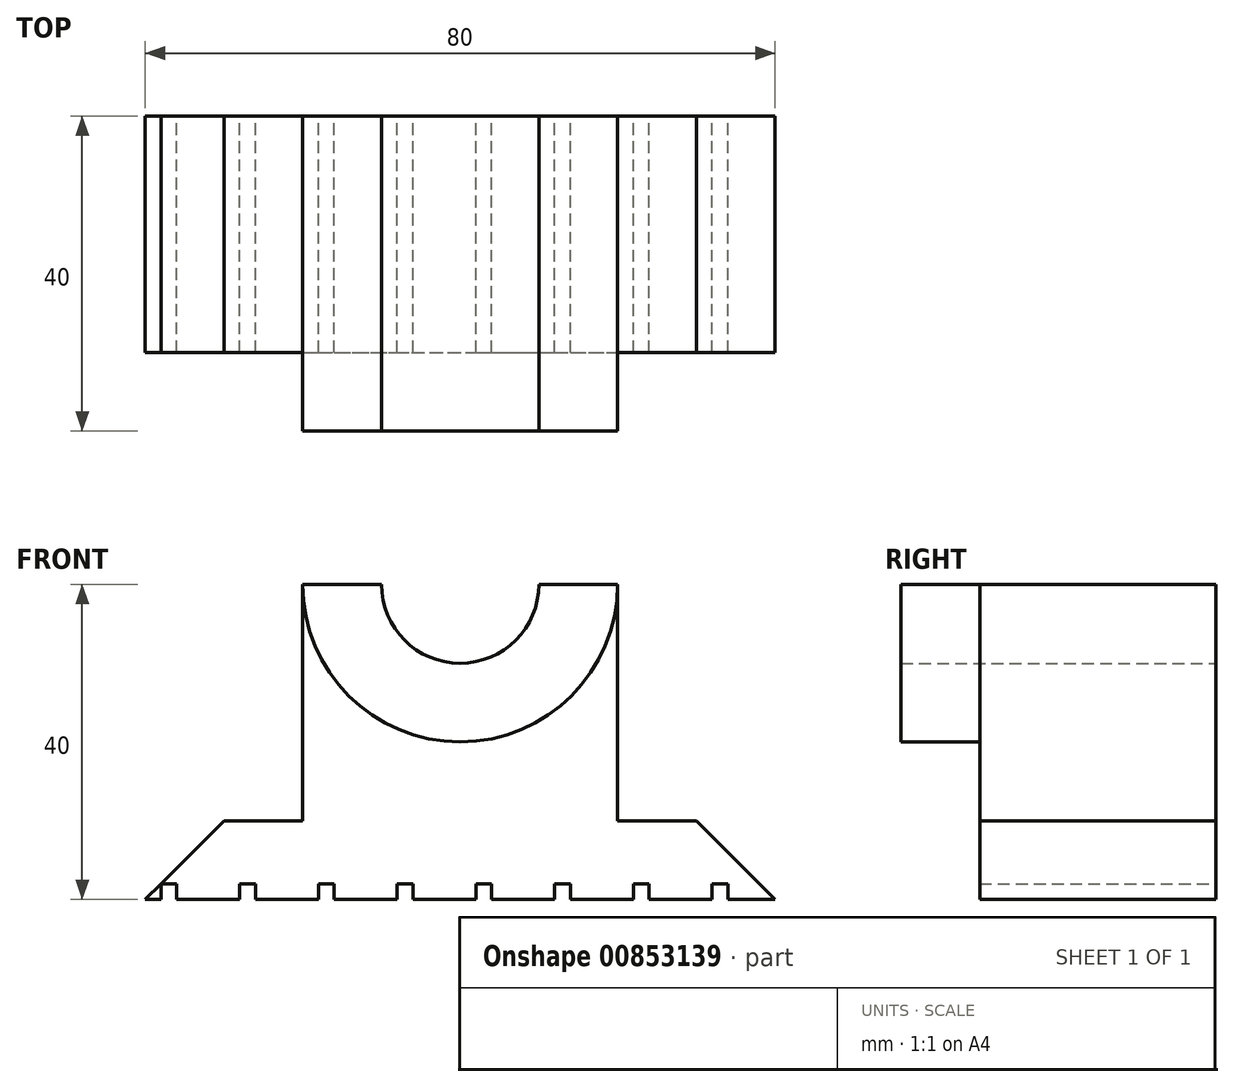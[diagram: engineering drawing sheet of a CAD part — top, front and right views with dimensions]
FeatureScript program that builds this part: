
annotation { "Feature Type Name" : "Feature", "Feature Type Description" : "" }
export const myFeature = defineFeature(function(context is Context, id is Id, definition is map)
    precondition{}
    {
        {
            var Q0;
            Q0=qCreatedBy(makeId("Front.planeOp"),FACE);
            var sketch = newSketch(context, id + "F0", { "sketchPlane" : qUnion([Q0])});
            skLineSegment(sketch, "E0", {"start": v(-40, 0) * mm, "end": v(40, 0) * mm});
            skLineSegment(sketch, "E1", {"start": v(40, 0) * mm, "end": v(30, 10) * mm});
            skLineSegment(sketch, "E2", {"start": v(30, 10) * mm, "end": v(20, 10) * mm});
            skLineSegment(sketch, "E3", {"start": v(20, 10) * mm, "end": v(20, 40) * mm});
            skLineSegment(sketch, "E4", {"start": v(20, 40) * mm, "end": v(10, 40) * mm});
            skLineSegment(sketch, "E5", {"start": v(-20, 40) * mm, "end": v(-20, 10) * mm});
            skLineSegment(sketch, "E6", {"start": v(-20, 10) * mm, "end": v(-30, 10) * mm});
            skLineSegment(sketch, "E7", {"start": v(-30, 10) * mm, "end": v(-40, 0) * mm});
            skArc(sketch, "E8", {"start": v(-10, 40) * mm, "mid": v(0, 30) * mm, "end": v(10, 40) * mm});
            skLineSegment(sketch, "E9.trimOffspring", {"start": v(-10, 40) * mm, "end": v(-20, 40) * mm});
            skSolve(sketch);
        }
        {
            var Q0;
            Q0 = qSketchRegion(id + "F0", true);
            extrude(context, id + "F1", {"entities" : qUnion([Q0]), "depth" : 30 * mm, "offsetDistance" : 25 * mm});
        }
        {
            var Q0;
            Q0=makeQuery(id+"F1.opExtrude","CAP_FACE",FACE,{"disambiguationData":[OSD([sQuery(id+"F0.wireOp",EDGE,"E0"),sQuery(id+"F0.wireOp",EDGE,"E1"),sQuery(id+"F0.wireOp",EDGE,"E2"),sQuery(id+"F0.wireOp",EDGE,"E3"),sQuery(id+"F0.wireOp",EDGE,"E4"),sQuery(id+"F0.wireOp",EDGE,"E5"),sQuery(id+"F0.wireOp",EDGE,"E6"),sQuery(id+"F0.wireOp",EDGE,"E7"),sQuery(id+"F0.wireOp",EDGE,"E8"),sQuery(id+"F0.wireOp",EDGE,"E9.trimOffspring")])],"isStart":false});
            var sketch = newSketch(context, id + "F2", { "sketchPlane" : qUnion([Q0])});
            skArc(sketch, "E10", {"start": v(-20, 40) * mm, "mid": v(0, 20) * mm, "end": v(20, 40) * mm});
            skArc(sketch, "E11", {"start": v(-10, 40) * mm, "mid": v(0, 30) * mm, "end": v(10, 40) * mm});
            skLineSegment(sketch, "E12", {"start": v(-20, 40) * mm, "end": v(-10, 40) * mm});
            skLineSegment(sketch, "E13.trimOffspring", {"start": v(10, 40) * mm, "end": v(20, 40) * mm});
            skSolve(sketch);
        }
        {
            var Q0;
            Q0 = qSketchRegion(id + "F2", true);
            extrude(context, id + "F3", {"entities" : qUnion([Q0]), "operationType" : NewBodyOperationType.ADD, "depth" : 10 * mm, "offsetDistance" : 25 * mm});
        }
        {
            var Q0;
            Q0=makeQuery(id+"F1.opExtrude","SWEPT_FACE",FACE,{"disambiguationData":[OSD([sQuery(id+"F0.wireOp",EDGE,"E0")])]});
            var sketch = newSketch(context, id + "F4", { "sketchPlane" : qUnion([Q0])});
            skLineSegment(sketch, "E14.bottom", {"start": v(-38, 30) * mm, "end": v(-36, 30) * mm});
            skLineSegment(sketch, "E14.top", {"start": v(-38, 0) * mm, "end": v(-36, 0) * mm});
            skLineSegment(sketch, "E14.left", {"start": v(-38, 30) * mm, "end": v(-38, 0) * mm});
            skLineSegment(sketch, "E14.right", {"start": v(-36, 30) * mm, "end": v(-36, 0) * mm});
            skLineSegment(sketch, "E15.1.0.0", {"start": v(-26, 30) * mm, "end": v(-26, 0) * mm});
            skLineSegment(sketch, "E15.1.0.1", {"start": v(-28, 30) * mm, "end": v(-28, 0) * mm});
            skLineSegment(sketch, "E15.1.0.2", {"start": v(-28, 30) * mm, "end": v(-26, 30) * mm});
            skLineSegment(sketch, "E15.1.0.3", {"start": v(-28, 0) * mm, "end": v(-26, 0) * mm});
            skLineSegment(sketch, "E15.2.0.0", {"start": v(-16, 30) * mm, "end": v(-16, 0) * mm});
            skLineSegment(sketch, "E15.2.0.1", {"start": v(-18, 30) * mm, "end": v(-18, 0) * mm});
            skLineSegment(sketch, "E15.2.0.2", {"start": v(-18, 30) * mm, "end": v(-16, 30) * mm});
            skLineSegment(sketch, "E15.2.0.3", {"start": v(-18, 0) * mm, "end": v(-16, 0) * mm});
            skLineSegment(sketch, "E15.3.0.0", {"start": v(-6, 30) * mm, "end": v(-6, 0) * mm});
            skLineSegment(sketch, "E15.3.0.1", {"start": v(-8, 30) * mm, "end": v(-8, 0) * mm});
            skLineSegment(sketch, "E15.3.0.2", {"start": v(-8, 30) * mm, "end": v(-6, 30) * mm});
            skLineSegment(sketch, "E15.3.0.3", {"start": v(-8, 0) * mm, "end": v(-6, 0) * mm});
            skLineSegment(sketch, "E15.4.0.0", {"start": v(4, 30) * mm, "end": v(4, 0) * mm});
            skLineSegment(sketch, "E15.4.0.1", {"start": v(2, 30) * mm, "end": v(2, 0) * mm});
            skLineSegment(sketch, "E15.4.0.2", {"start": v(2, 30) * mm, "end": v(4, 30) * mm});
            skLineSegment(sketch, "E15.4.0.3", {"start": v(2, 0) * mm, "end": v(4, 0) * mm});
            skLineSegment(sketch, "E15.5.0.0", {"start": v(14, 30) * mm, "end": v(14, 0) * mm});
            skLineSegment(sketch, "E15.5.0.1", {"start": v(12, 30) * mm, "end": v(12, 0) * mm});
            skLineSegment(sketch, "E15.5.0.2", {"start": v(12, 30) * mm, "end": v(14, 30) * mm});
            skLineSegment(sketch, "E15.5.0.3", {"start": v(12, 0) * mm, "end": v(14, 0) * mm});
            skLineSegment(sketch, "E15.6.0.0", {"start": v(24, 30) * mm, "end": v(24, 0) * mm});
            skLineSegment(sketch, "E15.6.0.1", {"start": v(22, 30) * mm, "end": v(22, 0) * mm});
            skLineSegment(sketch, "E15.6.0.2", {"start": v(22, 30) * mm, "end": v(24, 30) * mm});
            skLineSegment(sketch, "E15.6.0.3", {"start": v(22, 0) * mm, "end": v(24, 0) * mm});
            skLineSegment(sketch, "E15.7.0.0", {"start": v(34, 30) * mm, "end": v(34, 0) * mm});
            skLineSegment(sketch, "E15.7.0.1", {"start": v(32, 30) * mm, "end": v(32, 0) * mm});
            skLineSegment(sketch, "E15.7.0.2", {"start": v(32, 30) * mm, "end": v(34, 30) * mm});
            skLineSegment(sketch, "E15.7.0.3", {"start": v(32, 0) * mm, "end": v(34, 0) * mm});
            skLineSegment(sketch, "E15.direction1", {"start": v(-36, 0) * mm, "end": v(-26, 0) * mm, "construction": true});
            skSolve(sketch);
        }
        {
            var Q0;
            Q0=makeQuery(id+"F4.imprint","IMPRINT",FACE,{"disambiguationData":[TD([[makeQuery(id+"F4.imprint","IMPRINT",EDGE,{"derivedFrom":sQuery(id+"F4.wireOp",EDGE,"E15.1.0.0")}),-1.0]])]});
            var Q1;
            Q1=makeQuery(id+"F4.imprint","IMPRINT",FACE,{"disambiguationData":[TD([[makeQuery(id+"F4.imprint","IMPRINT",EDGE,{"derivedFrom":sQuery(id+"F4.wireOp",EDGE,"E14.bottom")}),-1.0]])]});
            var Q2;
            Q2=makeQuery(id+"F4.imprint","IMPRINT",FACE,{"disambiguationData":[TD([[makeQuery(id+"F4.imprint","IMPRINT",EDGE,{"derivedFrom":sQuery(id+"F4.wireOp",EDGE,"E15.2.0.0")}),-1.0]])]});
            var Q3;
            Q3=makeQuery(id+"F4.imprint","IMPRINT",FACE,{"disambiguationData":[TD([[makeQuery(id+"F4.imprint","IMPRINT",EDGE,{"derivedFrom":sQuery(id+"F4.wireOp",EDGE,"E15.3.0.0")}),-1.0]])]});
            var Q4;
            Q4=makeQuery(id+"F4.imprint","IMPRINT",FACE,{"disambiguationData":[TD([[makeQuery(id+"F4.imprint","IMPRINT",EDGE,{"derivedFrom":sQuery(id+"F4.wireOp",EDGE,"E15.4.0.0")}),-1.0]])]});
            var Q5;
            Q5=makeQuery(id+"F4.imprint","IMPRINT",FACE,{"disambiguationData":[TD([[makeQuery(id+"F4.imprint","IMPRINT",EDGE,{"derivedFrom":sQuery(id+"F4.wireOp",EDGE,"E15.5.0.0")}),-1.0]])]});
            var Q6;
            Q6=makeQuery(id+"F4.imprint","IMPRINT",FACE,{"disambiguationData":[TD([[makeQuery(id+"F4.imprint","IMPRINT",EDGE,{"derivedFrom":sQuery(id+"F4.wireOp",EDGE,"E15.6.0.0")}),-1.0]])]});
            var Q7;
            Q7=makeQuery(id+"F4.imprint","IMPRINT",FACE,{"disambiguationData":[TD([[makeQuery(id+"F4.imprint","IMPRINT",EDGE,{"derivedFrom":sQuery(id+"F4.wireOp",EDGE,"E15.7.0.0")}),-1.0]])]});
            var Q8;
            Q8 = qConstructionFilter(qBodyType(qCreatedBy(id + "F4" ,EDGE), BodyType.WIRE), ConstructionObject.NO);
            extrude(context, id + "F5", {"entities" : qUnion([Q0, Q1, Q2, Q3, Q4, Q5, Q6, Q7]), "operationType" : NewBodyOperationType.REMOVE, "surfaceEntities" : qUnion([Q8]), "oppositeDirection" : true, "depth" : 2 * mm, "offsetDistance" : 25 * mm});
        }
    });
